# Revit family: CONTURA II HANDSET
name_source: partatom
category: Plumbing Fixtures
units: mm (PartAtom-declared; Revit-internal decimal feet)

## family parameters
Cut with Voids When Loaded = No
Host = Face
OmniClass Number = 23.45.05.14.17
OmniClass Title = Showers
Part Type = Normal
Room Calculation Point = No
Round Connector Dimension = Use Diameter
Shared = No

## types (5) — shared parameters
CW Connection = No
HW Connection = No
Manufacturer = GWA Bathrooms & Kitchens
Material_Sprays = GWA-Plastic-General
URL = https://www.caroma.com.au
Vent Connection = No
Waste Connection = No
zero-valued in all types: Default Elevation

## per-type parameters (varying)
| type | Material | Material_Face | Model |
| CONTURA II HANDSET - CHROME | GWA_Metal-Chrome | GWA_Metal-Chrome | 849085C4A |
| CONTURA II HANDSET - MATTE BLACK | GWA-Metal-Black | GWA-Metal-Black | 849085B4A |
| CONTURA II HANDSET - BRUSHED BRASS | GWA_Metal-Brushed-Brass | GWA_Metal-Brushed-Brass | 849085BB4A |
| CONTURA II HANDSET - BRUSHED BRONZE | GWA_Metal-Brushed-Bronze | GWA_Metal-Brushed-Bronze | 849085BBZ4A |
| CONTURA II HANDSET - BRUSHED NICKEL | GWA_Metal-Brushed-Nickel | GWA_Metal-Brushed-Nickel | 849085BN4A |

note: column(s) folded — value = type name in every type: Description

## geometry (parser evidence)
native form markers: Blend x2, Sweep x3
no freeform markers — native parametric forms only
